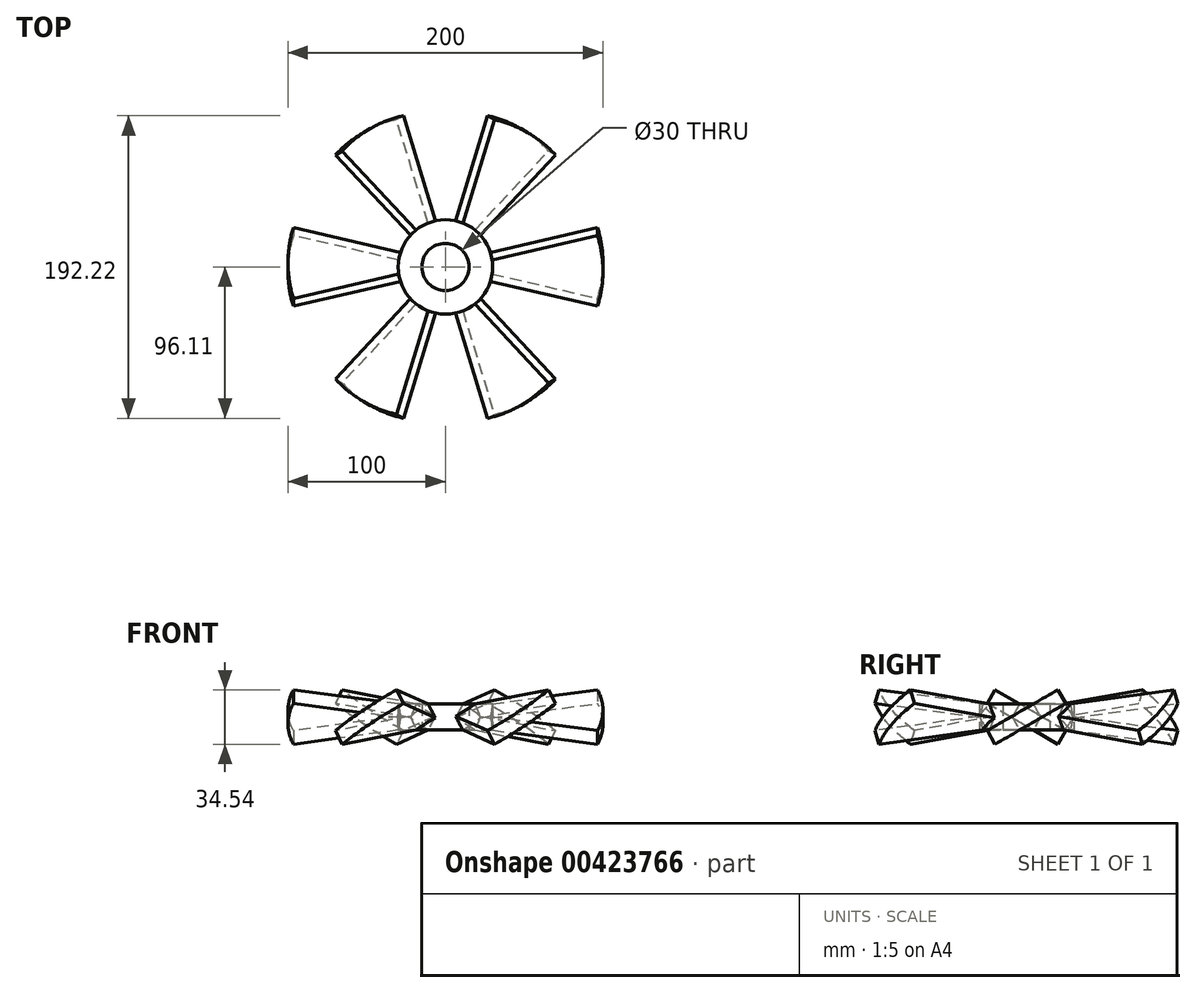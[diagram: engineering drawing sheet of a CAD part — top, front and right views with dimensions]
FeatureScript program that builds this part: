
annotation { "Feature Type Name" : "Feature", "Feature Type Description" : "" }
export const myFeature = defineFeature(function(context is Context, id is Id, definition is map)
    precondition{}
    {
        {
            var Q0;
            Q0=qCreatedBy(makeId("Top.planeOp"),FACE);
            var sketch = newSketch(context, id + "F0", { "sketchPlane" : qUnion([Q0])});
            skArc(sketch, "E0", {"start": v(96.6, -25.88) * mm, "mid": v(100, 0) * mm, "end": v(96.6, 25.88) * mm});
            skLineSegment(sketch, "E1", {"start": v(0, 0) * mm, "end": v(106.96, 0) * mm, "construction": true});
            skLineSegment(sketch, "E2", {"start": v(23.44, 6.28) * mm, "end": v(96.6, 25.88) * mm});
            skLineSegment(sketch, "E3.trimOffspring", {"start": v(23.44, -6.28) * mm, "end": v(96.6, -25.88) * mm});
            skCircle(sketch, "E4", {"center": v(0, 0) * mm, "radius": 15 * mm});
            skCircle(sketch, "E5", {"center": v(0, 0) * mm, "radius": 30 * mm});
            skArc(sketch, "E6", {"start": v(23.44, -6.28) * mm, "mid": v(24.27, 0) * mm, "end": v(23.44, 6.28) * mm});
            skSolve(sketch);
        }
        {
            var Q0;
            Q0=makeQuery(id+"F0.imprint","IMPRINT",FACE,{"disambiguationData":[TD([[makeQuery(id+"F0.imprint","IMPRINT",EDGE,{"derivedFrom":sQuery(id+"F0.wireOp",EDGE,"E0")}),1.0]])]});
            var Q1;
            {var subQ0=sQuery(id+"F0.wireOp",EDGE,"E6");Q1=makeQuery(id+"F0.imprint","IMPRINT",FACE,{"disambiguationData":[TD([[makeQuery(id+"F0.imprint","IMPRINT",EDGE,{"derivedFrom":subQ0}),-1.0]])]});}
            extrude(context, id + "F1", {"entities" : qUnion([Q0, Q1]), "endBound" : BoundingType.SYMMETRIC, "depth" : 10 * mm});
        }
        {
            var Q0;
            Q0=makeQuery(id+"F1.opExtrude","SWEPT_BODY",BODY,{"disambiguationData":[OSD([sQuery(id+"F0.wireOp",EDGE,"pdYgzSuy-1dPa-SH6e-YaA2-8cwxHsIPqGop"),sQuery(id+"F0.wireOp",EDGE,"E0"),sQuery(id+"F0.wireOp",EDGE,"E2"),sQuery(id+"F0.wireOp",EDGE,"E3.trimOffspring")])]});
            var Q1;
            Q1=sQuery(id+"F0.wireOp",EDGE,"E1");
            transform(context, id + "F2", {"entities" : qUnion([Q0]), "transformType" : TransformType.ROTATION, "transformAxis" : qUnion([Q1]), "angle" : 30 * degree, "makeCopy" : false});
        }
        {
            var Q0;
            Q0=qCreatedBy(makeId("Front.planeOp"),FACE);
            var sketch = newSketch(context, id + "F3", { "sketchPlane" : qUnion([Q0])});
            skLineSegment(sketch, "E7", {"start": v(0, 0) * mm, "end": v(0, 49.14) * mm, "construction": true});
            skSolve(sketch);
        }
        {
            var Q0;
            Q0=makeQuery(id+"F0.imprint","IMPRINT",FACE,{"disambiguationData":[TD([[makeQuery(id+"F0.imprint","IMPRINT",EDGE,{"derivedFrom":sQuery(id+"F0.wireOp",EDGE,"E4")}),-1.0]])]});
            var Q1;
            {var subQ0=sQuery(id+"F0.wireOp",EDGE,"E6");Q1=makeQuery(id+"F0.imprint","IMPRINT",FACE,{"disambiguationData":[TD([[makeQuery(id+"F0.imprint","IMPRINT",EDGE,{"derivedFrom":subQ0}),-1.0]])]});}
            extrude(context, id + "F4", {"entities" : qUnion([Q0, Q1]), "operationType" : NewBodyOperationType.REMOVE, "oppositeDirection" : true, "depth" : 25 * mm, "hasSecondDirection" : true, "secondDirectionOppositeDirection" : false, "secondDirectionDepth" : 25 * mm});
        }
        {
            var Q0;
            Q0=makeQuery(id+"F1.opExtrude","SWEPT_BODY",BODY,{"disambiguationData":[OSD([sQuery(id+"F0.wireOp",EDGE,"E0"),sQuery(id+"F0.wireOp",EDGE,"E2"),sQuery(id+"F0.wireOp",EDGE,"E3.trimOffspring"),sQuery(id+"F0.wireOp",EDGE,"E6")])]});
            var Q1;
            Q1=sQuery(id+"F3.wireOp",EDGE,"E7");
            circularPattern(context, id + "F5", {"entities" : qUnion([Q0]), "axis" : qUnion([Q1]), "angle" : 360 * degree, "instanceCount" : 6, "equalSpace" : true});
        }
        {
            var Q0;
            Q0=makeQuery(id+"F0.imprint","IMPRINT",FACE,{"disambiguationData":[TD([[makeQuery(id+"F0.imprint","IMPRINT",EDGE,{"derivedFrom":sQuery(id+"F0.wireOp",EDGE,"E4")}),-1.0]])]});
            var Q1;
            {var subQ0=sQuery(id+"F0.wireOp",EDGE,"E6");Q1=makeQuery(id+"F0.imprint","IMPRINT",FACE,{"disambiguationData":[TD([[makeQuery(id+"F0.imprint","IMPRINT",EDGE,{"derivedFrom":subQ0}),-1.0]])]});}
            var Q2;
            {var subQ0=sQuery(id+"F0.wireOp",EDGE,"E2");Q2=makeQuery(id+"F4.boolean.opBoolean","INTERSECT",VERTEX,{"derivedFrom":[makeQuery(id+"F1.opExtrude","CAP_FACE",FACE,{"disambiguationData":[OSD([sQuery(id+"F0.wireOp",EDGE,"E0"),subQ0,sQuery(id+"F0.wireOp",EDGE,"E3.trimOffspring"),sQuery(id+"F0.wireOp",EDGE,"E6")])],"isStart":false}),makeQuery(id+"F1.opExtrude","SWEPT_FACE",FACE,{"disambiguationData":[OSD([subQ0])]}),makeQuery(id+"F4.opExtrude","SWEPT_FACE",FACE,{"disambiguationData":[OSD([sQuery(id+"F0.wireOp",EDGE,"E5")])]})]});}
            var Q3;
            {var subQ0=sQuery(id+"F0.wireOp",EDGE,"E3.trimOffspring");Q3=makeQuery(id+"F4.boolean.opBoolean","INTERSECT",VERTEX,{"derivedFrom":[makeQuery(id+"F1.opExtrude","CAP_FACE",FACE,{"disambiguationData":[OSD([sQuery(id+"F0.wireOp",EDGE,"E0"),sQuery(id+"F0.wireOp",EDGE,"E2"),subQ0,sQuery(id+"F0.wireOp",EDGE,"E6")])],"isStart":true}),makeQuery(id+"F1.opExtrude","SWEPT_FACE",FACE,{"disambiguationData":[OSD([subQ0])]}),makeQuery(id+"F4.opExtrude","SWEPT_FACE",FACE,{"disambiguationData":[OSD([sQuery(id+"F0.wireOp",EDGE,"E5")])]})]});}
            extrude(context, id + "F6", {"entities" : qUnion([Q0, Q1]), "endBound" : BoundingType.UP_TO_VERTEX, "endBoundEntityVertex" : qUnion([Q2]), "depth" : 25 * mm, "hasSecondDirection" : true, "secondDirectionBound" : SecondDirectionBoundingType.UP_TO_VERTEX, "secondDirectionOppositeDirection" : true, "secondDirectionBoundEntityVertex" : qUnion([Q3]), "secondDirectionDepth" : 25 * mm});
        }
    });
